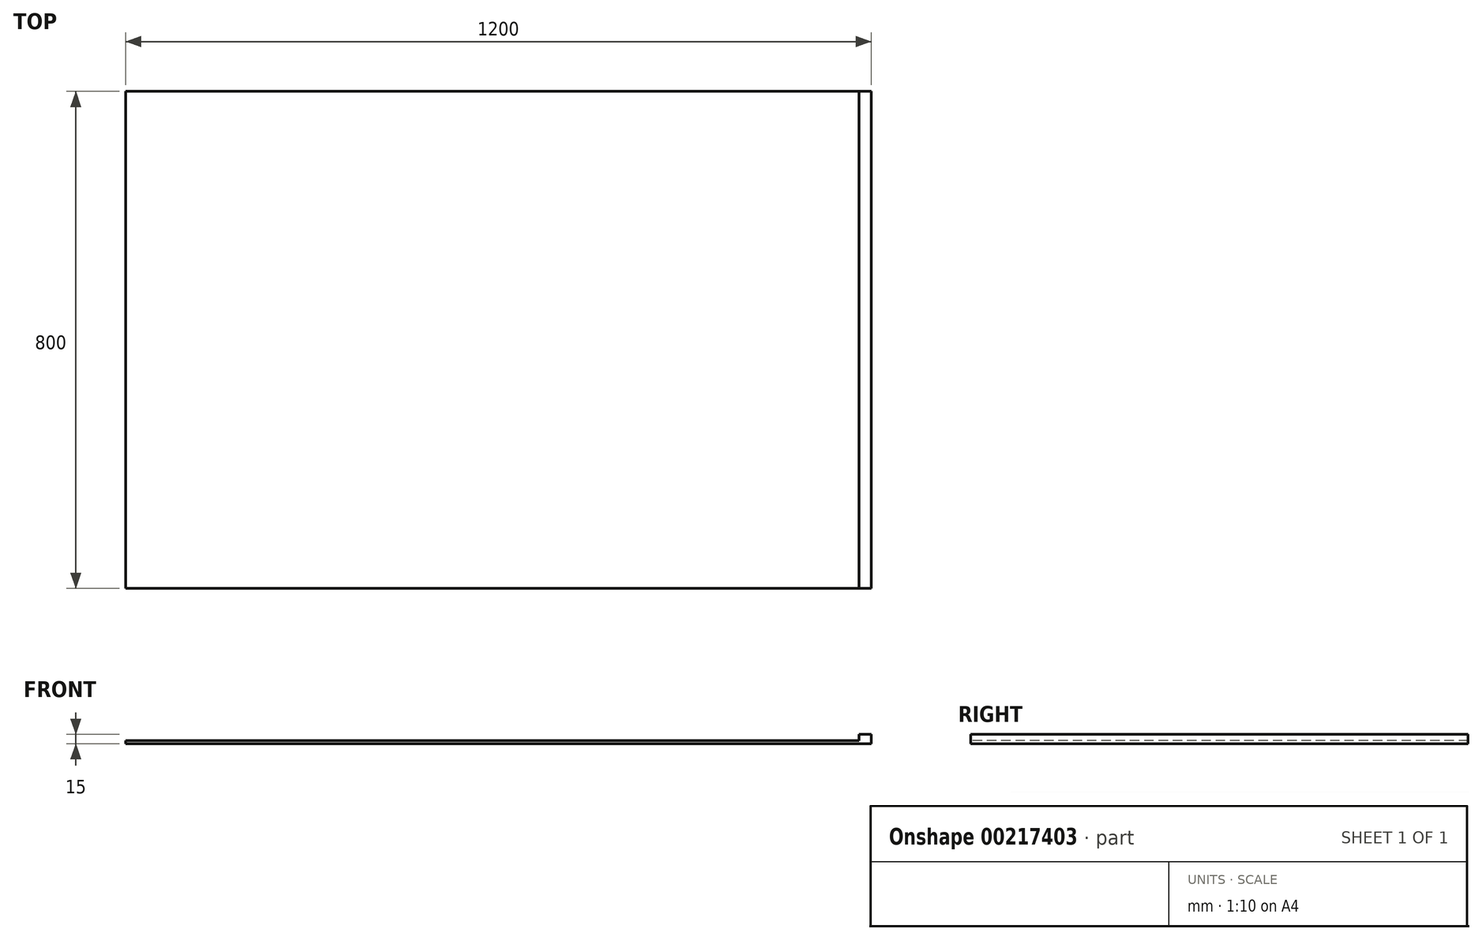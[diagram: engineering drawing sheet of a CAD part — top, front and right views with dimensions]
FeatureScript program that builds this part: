
annotation { "Feature Type Name" : "Feature", "Feature Type Description" : "" }
export const myFeature = defineFeature(function(context is Context, id is Id, definition is map)
    precondition{}
    {
        {
            var Q0;
            Q0=qCreatedBy(makeId("Top.planeOp"),FACE);
            var sketch = newSketch(context, id + "F0", { "sketchPlane" : qUnion([Q0])});
            skLineSegment(sketch, "E0.bottom", {"start": v(-620.16, 512.18) * mm, "end": v(579.84, 512.18) * mm});
            skLineSegment(sketch, "E0.top", {"start": v(-620.16, -287.82) * mm, "end": v(579.84, -287.82) * mm});
            skLineSegment(sketch, "E0.left", {"start": v(-620.16, 512.18) * mm, "end": v(-620.16, -287.82) * mm});
            skLineSegment(sketch, "E0.right", {"start": v(579.84, 512.18) * mm, "end": v(579.84, -287.82) * mm});
            skSolve(sketch);
        }
        {
            var Q0;
            Q0=makeQuery(id+"F0.imprint","IMPRINT",FACE,{"disambiguationData":[TD([[makeQuery(id+"F0.imprint","IMPRINT",EDGE,{"derivedFrom":sQuery(id+"F0.wireOp",EDGE,"E0.bottom")}),-1.0]])]});
            extrude(context, id + "F1", {"entities" : qUnion([Q0]), "endBound" : BoundingType.SYMMETRIC, "depth" : 5 * mm});
        }
        {
            var Q0;
            Q0=makeQuery(id+"F1.opExtrude","CAP_FACE",FACE,{"disambiguationData":[OSD([sQuery(id+"F0.wireOp",EDGE,"E0.bottom"),sQuery(id+"F0.wireOp",EDGE,"E0.top"),sQuery(id+"F0.wireOp",EDGE,"E0.left"),sQuery(id+"F0.wireOp",EDGE,"E0.right")])],"isStart":false});
            var sketch = newSketch(context, id + "F2", { "sketchPlane" : qUnion([Q0])});
            skLineSegment(sketch, "E1.bottom", {"start": v(579.84, 512.18) * mm, "end": v(559.84, 512.18) * mm});
            skLineSegment(sketch, "E1.top", {"start": v(579.84, -287.82) * mm, "end": v(559.84, -287.82) * mm});
            skLineSegment(sketch, "E1.left", {"start": v(579.84, 512.18) * mm, "end": v(579.84, -287.82) * mm});
            skLineSegment(sketch, "E1.right", {"start": v(559.84, 512.18) * mm, "end": v(559.84, -287.82) * mm});
            skSolve(sketch);
        }
        {
            var Q0;
            Q0=makeQuery(id+"F2.imprint","IMPRINT",FACE,{"disambiguationData":[TD([[makeQuery(id+"F2.imprint","IMPRINT",EDGE,{"derivedFrom":sQuery(id+"F2.wireOp",EDGE,"E1.bottom")}),-1.0]])]});
            extrude(context, id + "F3", {"entities" : qUnion([Q0]), "operationType" : NewBodyOperationType.ADD, "depth" : 10 * mm});
        }
    });
